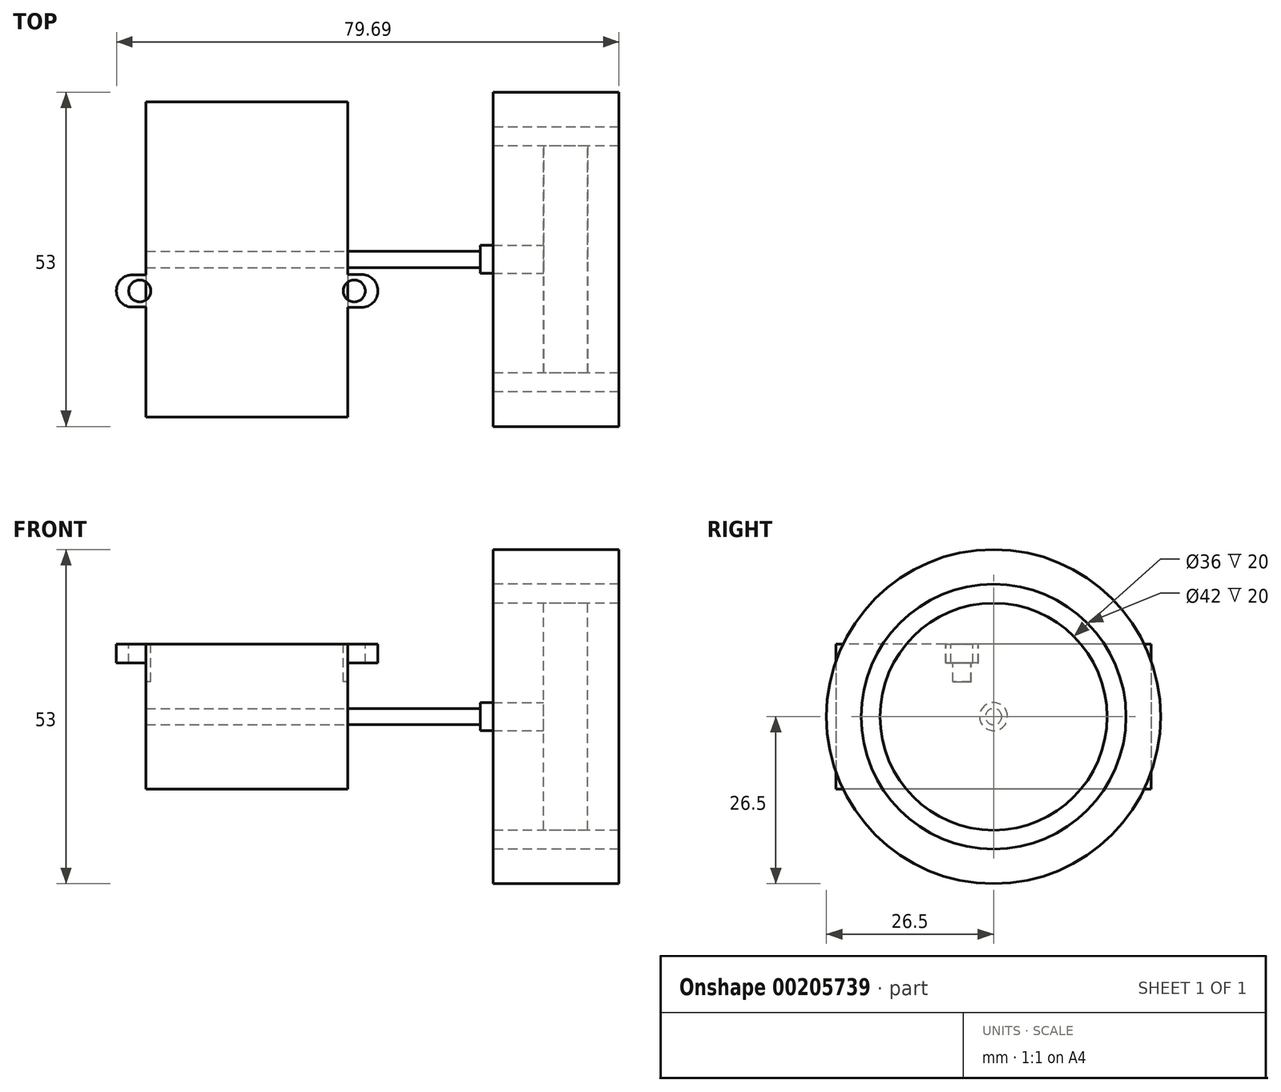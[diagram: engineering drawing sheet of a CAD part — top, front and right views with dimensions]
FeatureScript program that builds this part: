
annotation { "Feature Type Name" : "Feature", "Feature Type Description" : "" }
export const myFeature = defineFeature(function(context is Context, id is Id, definition is map)
    precondition{}
    {
        {
            var Q0;
            Q0=qCreatedBy(makeId("Right.planeOp"),FACE);
            var sketch = newSketch(context, id + "F0", { "sketchPlane" : qUnion([Q0])});
            skCircle(sketch, "E0", {"center": v(0, 0) * mm, "radius": 21 * mm});
            skCircle(sketch, "E1", {"center": v(0, 0) * mm, "radius": 26.5 * mm});
            skCircle(sketch, "E2", {"center": v(0, 0) * mm, "radius": 18 * mm});
            skPoint(sketch, "E3", {"position": v(0, 21) * mm});
            skSolve(sketch);
        }
        {
            var Q0;
            Q0 = qSketchRegion(id + "F0", true);
            extrude(context, id + "F1", {"entities" : qUnion([Q0]), "endBound" : BoundingType.SYMMETRIC, "depth" : 20 * mm});
        }
        {
            var Q0;
            Q0=qCreatedBy(makeId("Right.planeOp"),FACE);
            var sketch = newSketch(context, id + "F2", { "sketchPlane" : qUnion([Q0])});
            skCircle(sketch, "E4", {"center": v(0, 0) * mm, "radius": 21 * mm});
            skCircle(sketch, "E5", {"center": v(0, 0) * mm, "radius": 18 * mm});
            skPoint(sketch, "E6", {"position": v(-18, 0) * mm});
            skSolve(sketch);
        }
        {
            var Q0;
            Q0 = qSketchRegion(id + "F2", true);
            extrude(context, id + "F3", {"entities" : qUnion([Q0]), "endBound" : BoundingType.SYMMETRIC, "depth" : 20 * mm});
        }
        {
            var Q0;
            Q0=qCreatedBy(makeId("Right.planeOp"),FACE);
            var sketch = newSketch(context, id + "F4", { "sketchPlane" : qUnion([Q0])});
            skCircle(sketch, "E7", {"center": v(0, 0) * mm, "radius": 18 * mm});
            skPoint(sketch, "E8", {"position": v(0, 18) * mm});
            skSolve(sketch);
        }
        {
            var Q0;
            Q0 = qSketchRegion(id + "F4", true);
            extrude(context, id + "F5", {"entities" : qUnion([Q0]), "depth" : 5 * mm, "hasSecondDirection" : true, "secondDirectionOppositeDirection" : true, "secondDirectionDepth" : 2 * mm});
        }
        {
            var Q0;
            Q0=qCreatedBy(makeId("Right.planeOp"),FACE);
            var sketch = newSketch(context, id + "F6", { "sketchPlane" : qUnion([Q0])});
            skCircle(sketch, "E9", {"center": v(0, 0) * mm, "radius": 2.22 * mm});
            skCircle(sketch, "E10", {"center": v(0, 0) * mm, "radius": 1.3 * mm});
            skSolve(sketch);
        }
        {
            var Q0;
            Q0 = qSketchRegion(id + "F6", true);
            extrude(context, id + "F7", {"entities" : qUnion([Q0]), "operationType" : NewBodyOperationType.ADD, "oppositeDirection" : true, "depth" : 12 * mm});
        }
        {
            var Q0;
            Q0=makeQuery(id+"F7.boolean.opBoolean","SPLIT",FACE,{"disambiguationData":[TD([makeQuery(id+"F7.opExtrude","SWEPT_FACE",FACE,{"disambiguationData":[OSD([sQuery(id+"F6.wireOp",EDGE,"E10")])]})])],"derivedFrom":makeQuery(id+"F5.opExtrude","CAP_FACE",FACE,{"disambiguationData":[OSD([sQuery(id+"F4.wireOp",EDGE,"E7")])],"isStart":true})});
            extrude(context, id + "F8", {"entities" : qUnion([Q0]), "operationType" : NewBodyOperationType.ADD, "depth" : 31 * mm});
        }
        {
            var Q0;
            Q0=makeQuery(id+"F8.opExtrude","CAP_FACE",FACE,{"disambiguationData":[OSD([sQuery(id+"F4.wireOp",EDGE,"E7")])],"isStart":false});
            var sketch = newSketch(context, id + "F9", { "sketchPlane" : qUnion([Q0])});
            skLineSegment(sketch, "E11.bottom", {"start": v(-25, 11.5) * mm, "end": v(25, 11.5) * mm});
            skLineSegment(sketch, "E11.top", {"start": v(-25, -11.5) * mm, "end": v(25, -11.5) * mm});
            skLineSegment(sketch, "E11.left", {"start": v(-25, 11.5) * mm, "end": v(-25, -11.5) * mm});
            skLineSegment(sketch, "E11.right", {"start": v(25, 11.5) * mm, "end": v(25, -11.5) * mm});
            skPoint(sketch, "E11.middle", {"position": v(0, 0) * mm});
            skSolve(sketch);
        }
        {
            var Q0;
            Q0=makeQuery(id+"F9.imprint","IMPRINT",FACE,{"disambiguationData":[TD([[makeQuery(id+"F9.imprint","IMPRINT",EDGE,{"derivedFrom":sQuery(id+"F9.wireOp",EDGE,"E11.bottom")}),-1.0]])]});
            extrude(context, id + "F10", {"entities" : qUnion([Q0]), "depth" : 32 * mm});
        }
        {
            var Q0;
            Q0=makeQuery(id+"F10.opExtrude","SWEPT_FACE",FACE,{"disambiguationData":[OSD([sQuery(id+"F9.wireOp",EDGE,"E11.bottom")])]});
            var sketch = newSketch(context, id + "F11", { "sketchPlane" : qUnion([Q0])});
            skLineSegment(sketch, "E12", {"start": v(-33, 0) * mm, "end": v(-65, 0) * mm, "construction": true});
            skLineSegment(sketch, "E13", {"start": v(-35.02, 0) * mm, "end": v(-35.02, -5) * mm, "construction": true});
            skCircle(sketch, "E14", {"center": v(-32, -5) * mm, "radius": 1.75 * mm});
            skLineSegment(sketch, "E15", {"start": v(-33.74, -5) * mm, "end": v(-30.24, -5) * mm, "construction": true});
            skCircle(sketch, "E16", {"center": v(-66, -5) * mm, "radius": 1.75 * mm});
            skLineSegment(sketch, "E17", {"start": v(-64.24, -5) * mm, "end": v(-67.74, -5) * mm, "construction": true});
            skLineSegment(sketch, "E18.bottom", {"start": v(-35.7, -2.4) * mm, "end": v(-30.77, -2.4) * mm});
            skLineSegment(sketch, "E18.top", {"start": v(-35.7, -7.6) * mm, "end": v(-30.77, -7.6) * mm});
            skLineSegment(sketch, "E18.left", {"start": v(-35.7, -2.4) * mm, "end": v(-35.7, -7.6) * mm});
            skLineSegment(sketch, "E18.right", {"start": v(-28.27, -4.9) * mm, "end": v(-28.27, -5.1) * mm});
            skPoint(sketch, "E19.visualSharp", {"position": v(-28.27, -2.4) * mm});
            skArc(sketch, "E19.filletArc", {"start": v(-28.27, -4.9) * mm, "mid": v(-29, -3.13) * mm, "end": v(-30.77, -2.4) * mm});
            skPoint(sketch, "E20.visualSharp", {"position": v(-28.27, -7.6) * mm});
            skArc(sketch, "E20.filletArc", {"start": v(-30.77, -7.6) * mm, "mid": v(-29, -6.87) * mm, "end": v(-28.27, -5.1) * mm});
            skLineSegment(sketch, "E21.bottom", {"start": v(-67.2, -2.44) * mm, "end": v(-62.3, -2.44) * mm});
            skLineSegment(sketch, "E21.top", {"start": v(-67.2, -7.56) * mm, "end": v(-62.3, -7.56) * mm});
            skLineSegment(sketch, "E21.left", {"start": v(-69.7, -4.94) * mm, "end": v(-69.7, -5.06) * mm});
            skLineSegment(sketch, "E21.right", {"start": v(-62.3, -2.44) * mm, "end": v(-62.3, -7.56) * mm});
            skPoint(sketch, "E22.visualSharp", {"position": v(-69.7, -2.44) * mm});
            skArc(sketch, "E22.filletArc", {"start": v(-67.2, -2.44) * mm, "mid": v(-68.96, -3.17) * mm, "end": v(-69.7, -4.94) * mm});
            skPoint(sketch, "E23.visualSharp", {"position": v(-69.7, -7.56) * mm});
            skArc(sketch, "E23.filletArc", {"start": v(-69.7, -5.06) * mm, "mid": v(-68.96, -6.83) * mm, "end": v(-67.2, -7.56) * mm});
            skLineSegment(sketch, "E24", {"start": v(-49, 0) * mm, "end": v(-49, -25) * mm, "construction": true});
            skLineSegment(sketch, "E25", {"start": v(-62.3, -5) * mm, "end": v(-49, -5) * mm, "construction": true});
            skLineSegment(sketch, "E26", {"start": v(-49, -5) * mm, "end": v(-35.7, -5) * mm, "construction": true});
            skSolve(sketch);
        }
        {
            var Q0;
            {var subQ0=sQuery(id+"F11.wireOp",EDGE,"E16");var subQ1=makeQuery(id+"F10.opExtrude","CAP_EDGE",EDGE,{"disambiguationData":[OSD([sQuery(id+"F9.wireOp",EDGE,"E11.bottom")])],"isStart":false});var subQ2=makeQuery(id+"F11.imprint","INTERSECT",VERTEX,{"disambiguationData":[OD(0.0)],"derivedFrom":[subQ1,subQ0]});Q0=makeQuery(id+"F11.imprint","IMPRINT",FACE,{"disambiguationData":[TD([[makeQuery(id+"F11.imprint","IMPRINT",EDGE,{"disambiguationData":[TD([[subQ2,1.0]])],"derivedFrom":subQ0}),1.0]])]});}
            var Q1;
            Q1=sQuery(id+"F11.wireOp",EDGE,"E16");
            extrude(context, id + "F12", {"entities" : qUnion([Q0]), "operationType" : NewBodyOperationType.REMOVE, "surfaceEntities" : qUnion([Q1]), "oppositeDirection" : true, "depth" : 6 * mm});
        }
        {
            var Q0;
            Q0=makeQuery(id+"F11.imprint","IMPRINT",FACE,{"disambiguationData":[TD([[makeQuery(id+"F11.imprint","IMPRINT",EDGE,{"derivedFrom":sQuery(id+"F11.wireOp",EDGE,"E21.left")}),1.0]])]});
            extrude(context, id + "F13", {"entities" : qUnion([Q0]), "operationType" : NewBodyOperationType.ADD, "oppositeDirection" : true, "depth" : 3 * mm});
        }
        {
            var Q0;
            {var subQ0=sQuery(id+"F11.wireOp",EDGE,"E14");var subQ1=makeQuery(id+"F10.opExtrude","CAP_EDGE",EDGE,{"disambiguationData":[OSD([sQuery(id+"F9.wireOp",EDGE,"E11.bottom")])],"isStart":true});var subQ2=makeQuery(id+"F11.imprint","INTERSECT",VERTEX,{"disambiguationData":[OD(0.0)],"derivedFrom":[subQ1,subQ0]});Q0=makeQuery(id+"F11.imprint","IMPRINT",FACE,{"disambiguationData":[TD([[makeQuery(id+"F11.imprint","IMPRINT",EDGE,{"disambiguationData":[TD([[subQ2,-1.0]])],"derivedFrom":subQ0}),1.0]])]});}
            extrude(context, id + "F14", {"entities" : qUnion([Q0]), "operationType" : NewBodyOperationType.REMOVE, "oppositeDirection" : true, "depth" : 6 * mm});
        }
        {
            var Q0;
            Q0=makeQuery(id+"F11.imprint","IMPRINT",FACE,{"disambiguationData":[TD([[makeQuery(id+"F11.imprint","IMPRINT",EDGE,{"derivedFrom":sQuery(id+"F11.wireOp",EDGE,"E18.right")}),-1.0]])]});
            extrude(context, id + "F15", {"entities" : qUnion([Q0]), "operationType" : NewBodyOperationType.ADD, "oppositeDirection" : true, "depth" : 3 * mm});
        }
    });
